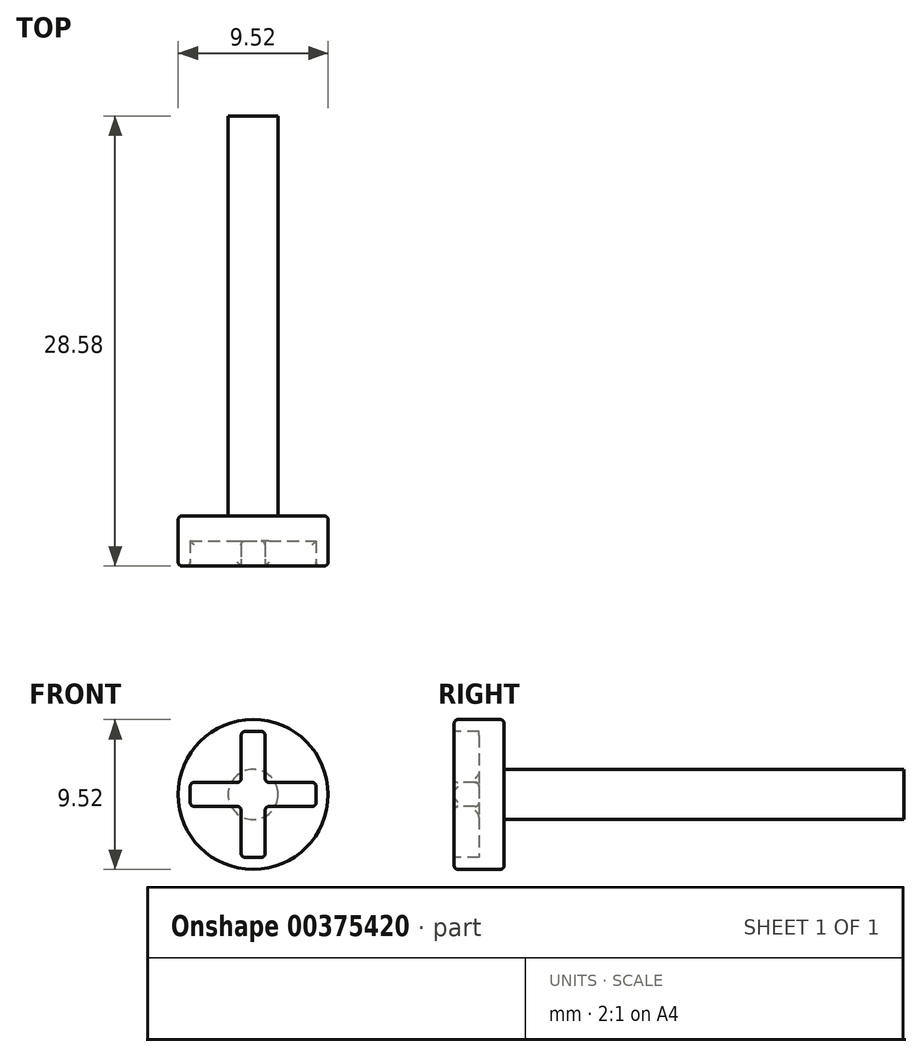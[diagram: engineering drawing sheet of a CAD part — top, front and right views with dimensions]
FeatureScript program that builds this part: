
annotation { "Feature Type Name" : "Feature", "Feature Type Description" : "" }
export const myFeature = defineFeature(function(context is Context, id is Id, definition is map)
    precondition{}
    {
        {
            var Q0;
            Q0=qCreatedBy(makeId("Front.planeOp"),FACE);
            var sketch = newSketch(context, id + "F0", { "sketchPlane" : qUnion([Q0])});
            skCircle(sketch, "E0", {"center": v(0, 0) * mm, "radius": 1.59 * mm});
            skSolve(sketch);
        }
        {
            var Q0;
            Q0=qSketchRegion(id+"F0",true);
            extrude(context, id + "F1", {"entities" : qUnion([Q0]), "depth" : 25.4 * mm, "symmetric" : true});
        }
        {
            var Q0;
            Q0=makeQuery(id+"F1.opExtrude","CAP_FACE",FACE,{"disambiguationData":[OSD([sQuery(id+"F0.wireOp",EDGE,"E0")])],"isStart":false});
            var sketch = newSketch(context, id + "F2", { "sketchPlane" : qUnion([Q0])});
            skCircle(sketch, "E1", {"center": v(0, 0) * mm, "radius": 4.76 * mm});
            skSolve(sketch);
        }
        {
            var Q0;
            Q0=qSketchRegion(id+"F2",true);
            extrude(context, id + "F3", {"entities" : qUnion([Q0]), "operationType" : NewBodyOperationType.ADD, "depth" : 3.17 * mm});
        }
        {
            var Q0;
            Q0=makeQuery(id+"F3.opExtrude","CAP_FACE",FACE,{"disambiguationData":[OSD([sQuery(id+"F2.wireOp",EDGE,"E1")])],"isStart":false});
            var sketch = newSketch(context, id + "F4", { "sketchPlane" : qUnion([Q0])});
            skLineSegment(sketch, "E2.bottom", {"start": v(-0.76, 4) * mm, "end": v(0.76, 4) * mm});
            skLineSegment(sketch, "E2.top", {"start": v(-0.76, -4) * mm, "end": v(0.76, -4) * mm});
            skLineSegment(sketch, "E2.left", {"start": v(-0.76, 4) * mm, "end": v(-0.76, -4) * mm});
            skLineSegment(sketch, "E2.right", {"start": v(0.76, 4) * mm, "end": v(0.76, -4) * mm});
            skLineSegment(sketch, "E3.bottom", {"start": v(-4, 0.76) * mm, "end": v(4, 0.76) * mm});
            skLineSegment(sketch, "E3.top", {"start": v(-4, -0.76) * mm, "end": v(4, -0.76) * mm});
            skLineSegment(sketch, "E3.left", {"start": v(-4, 0.76) * mm, "end": v(-4, -0.76) * mm});
            skLineSegment(sketch, "E3.right", {"start": v(4, 0.76) * mm, "end": v(4, -0.76) * mm});
            skSolve(sketch);
        }
        {
            var Q0;
            Q0=qSketchRegion(id+"F4",true);
            extrude(context, id + "F5", {"entities" : qUnion([Q0]), "operationType" : NewBodyOperationType.REMOVE, "oppositeDirection" : true, "depth" : 1.59 * mm});
        }
        {
            var Q0;
            Q0=makeQuery(id+"F3.opExtrude","CAP_EDGE",EDGE,{"disambiguationData":[OSD([sQuery(id+"F2.wireOp",EDGE,"E1")])],"isStart":false});
            var Q1;
            {var subQ0=sQuery(id+"F4.wireOp",EDGE,"E3.bottom");Q1=makeQuery(id+"F5.boolean.opBoolean","COPY",EDGE,{"derivedFrom":makeQuery(id+"F5.opExtrude","CAP_EDGE",EDGE,{"disambiguationData":[OSD([subQ0]),TDD([makeQuery(id+"F4.imprint","IMPRINT",EDGE,{"disambiguationData":[TD([[makeQuery(id+"F4.imprint","INTERSECT",VERTEX,{"derivedFrom":[subQ0,sQuery(id+"F4.wireOp",EDGE,"E3.left")]}),-1.0]])],"derivedFrom":subQ0})])],"isStart":true})});}
            var Q2;
            {var subQ0=sQuery(id+"F4.wireOp",EDGE,"E2.left");Q2=makeQuery(id+"F5.boolean.opBoolean","COPY",EDGE,{"derivedFrom":makeQuery(id+"F5.opExtrude","CAP_EDGE",EDGE,{"disambiguationData":[OSD([subQ0]),TDD([makeQuery(id+"F4.imprint","IMPRINT",EDGE,{"disambiguationData":[TD([[makeQuery(id+"F4.imprint","INTERSECT",VERTEX,{"derivedFrom":[sQuery(id+"F4.wireOp",EDGE,"E2.bottom"),subQ0]}),-1.0]])],"derivedFrom":subQ0})])],"isStart":true})});}
            var Q3;
            {var subQ0=sQuery(id+"F4.wireOp",EDGE,"E2.right");Q3=makeQuery(id+"F5.boolean.opBoolean","COPY",EDGE,{"derivedFrom":makeQuery(id+"F5.opExtrude","CAP_EDGE",EDGE,{"disambiguationData":[OSD([subQ0]),TDD([makeQuery(id+"F4.imprint","IMPRINT",EDGE,{"disambiguationData":[TD([[makeQuery(id+"F4.imprint","INTERSECT",VERTEX,{"derivedFrom":[sQuery(id+"F4.wireOp",EDGE,"E2.bottom"),subQ0]}),-1.0]])],"derivedFrom":subQ0})])],"isStart":true})});}
            var Q4;
            {var subQ0=sQuery(id+"F4.wireOp",EDGE,"E3.top");Q4=makeQuery(id+"F5.boolean.opBoolean","COPY",EDGE,{"derivedFrom":makeQuery(id+"F5.opExtrude","CAP_EDGE",EDGE,{"disambiguationData":[OSD([subQ0]),TDD([makeQuery(id+"F4.imprint","IMPRINT",EDGE,{"disambiguationData":[TD([[makeQuery(id+"F4.imprint","INTERSECT",VERTEX,{"derivedFrom":[subQ0,sQuery(id+"F4.wireOp",EDGE,"E3.left")]}),-1.0]])],"derivedFrom":subQ0})])],"isStart":true})});}
            var Q5;
            {var subQ0=sQuery(id+"F4.wireOp",EDGE,"E2.left");Q5=makeQuery(id+"F5.boolean.opBoolean","COPY",EDGE,{"derivedFrom":makeQuery(id+"F5.opExtrude","CAP_EDGE",EDGE,{"disambiguationData":[OSD([subQ0]),TDD([makeQuery(id+"F4.imprint","IMPRINT",EDGE,{"disambiguationData":[TD([[makeQuery(id+"F4.imprint","INTERSECT",VERTEX,{"derivedFrom":[sQuery(id+"F4.wireOp",EDGE,"E2.top"),subQ0]}),1.0]])],"derivedFrom":subQ0})])],"isStart":true})});}
            var Q6;
            {var subQ0=sQuery(id+"F4.wireOp",EDGE,"E3.top");Q6=makeQuery(id+"F5.boolean.opBoolean","COPY",EDGE,{"derivedFrom":makeQuery(id+"F5.opExtrude","CAP_EDGE",EDGE,{"disambiguationData":[OSD([subQ0]),TDD([makeQuery(id+"F4.imprint","IMPRINT",EDGE,{"disambiguationData":[TD([[makeQuery(id+"F4.imprint","INTERSECT",VERTEX,{"derivedFrom":[subQ0,sQuery(id+"F4.wireOp",EDGE,"E3.right")]}),1.0]])],"derivedFrom":subQ0})])],"isStart":true})});}
            var Q7;
            {var subQ0=sQuery(id+"F4.wireOp",EDGE,"E3.bottom");Q7=makeQuery(id+"F5.boolean.opBoolean","COPY",EDGE,{"derivedFrom":makeQuery(id+"F5.opExtrude","CAP_EDGE",EDGE,{"disambiguationData":[OSD([subQ0]),TDD([makeQuery(id+"F4.imprint","IMPRINT",EDGE,{"disambiguationData":[TD([[makeQuery(id+"F4.imprint","INTERSECT",VERTEX,{"derivedFrom":[subQ0,sQuery(id+"F4.wireOp",EDGE,"E3.right")]}),1.0]])],"derivedFrom":subQ0})])],"isStart":true})});}
            var Q8;
            {var subQ0=sQuery(id+"F4.wireOp",EDGE,"E3.bottom");Q8=makeQuery(id+"F5.boolean.opBoolean","COPY",FACE,{"derivedFrom":makeQuery(id+"F5.opExtrude","SWEPT_FACE",FACE,{"disambiguationData":[OSD([subQ0]),TDD([makeQuery(id+"F4.imprint","IMPRINT",EDGE,{"disambiguationData":[TD([[makeQuery(id+"F4.imprint","INTERSECT",VERTEX,{"derivedFrom":[subQ0,sQuery(id+"F4.wireOp",EDGE,"E3.left")]}),-1.0]])],"derivedFrom":subQ0})])]})});}
            var Q9;
            {var subQ0=sQuery(id+"F4.wireOp",EDGE,"E3.bottom");Q9=makeQuery(id+"F5.boolean.opBoolean","COPY",FACE,{"derivedFrom":makeQuery(id+"F5.opExtrude","SWEPT_FACE",FACE,{"disambiguationData":[OSD([subQ0]),TDD([makeQuery(id+"F4.imprint","IMPRINT",EDGE,{"disambiguationData":[TD([[makeQuery(id+"F4.imprint","INTERSECT",VERTEX,{"derivedFrom":[subQ0,sQuery(id+"F4.wireOp",EDGE,"E3.right")]}),1.0]])],"derivedFrom":subQ0})])]})});}
            var Q10;
            {var subQ0=sQuery(id+"F4.wireOp",EDGE,"E3.top");Q10=makeQuery(id+"F5.boolean.opBoolean","COPY",FACE,{"derivedFrom":makeQuery(id+"F5.opExtrude","SWEPT_FACE",FACE,{"disambiguationData":[OSD([subQ0]),TDD([makeQuery(id+"F4.imprint","IMPRINT",EDGE,{"disambiguationData":[TD([[makeQuery(id+"F4.imprint","INTERSECT",VERTEX,{"derivedFrom":[subQ0,sQuery(id+"F4.wireOp",EDGE,"E3.left")]}),-1.0]])],"derivedFrom":subQ0})])]})});}
            var Q11;
            {var subQ0=sQuery(id+"F4.wireOp",EDGE,"E3.top");Q11=makeQuery(id+"F5.boolean.opBoolean","COPY",FACE,{"derivedFrom":makeQuery(id+"F5.opExtrude","SWEPT_FACE",FACE,{"disambiguationData":[OSD([subQ0]),TDD([makeQuery(id+"F4.imprint","IMPRINT",EDGE,{"disambiguationData":[TD([[makeQuery(id+"F4.imprint","INTERSECT",VERTEX,{"derivedFrom":[subQ0,sQuery(id+"F4.wireOp",EDGE,"E3.right")]}),1.0]])],"derivedFrom":subQ0})])]})});}
            var Q12;
            Q12=makeQuery(id+"F5.boolean.opBoolean","COPY",EDGE,{"derivedFrom":makeQuery(id+"F5.opExtrude","CAP_EDGE",EDGE,{"disambiguationData":[OSD([sQuery(id+"F4.wireOp",EDGE,"E2.bottom")])],"isStart":true})});
            var Q13;
            Q13=makeQuery(id+"F5.boolean.opBoolean","COPY",EDGE,{"derivedFrom":makeQuery(id+"F5.opExtrude","CAP_EDGE",EDGE,{"disambiguationData":[OSD([sQuery(id+"F4.wireOp",EDGE,"E2.top")])],"isStart":true})});
            var Q14;
            Q14=makeQuery(id+"F5.boolean.opBoolean","COPY",EDGE,{"derivedFrom":makeQuery(id+"F5.opExtrude","SWEPT_EDGE",EDGE,{"disambiguationData":[OSD([sQuery(id+"F4.wireOp",EDGE,"E2.bottom"),sQuery(id+"F4.wireOp",EDGE,"E2.right")])]})});
            var Q15;
            Q15=makeQuery(id+"F5.boolean.opBoolean","COPY",EDGE,{"derivedFrom":makeQuery(id+"F5.opExtrude","SWEPT_EDGE",EDGE,{"disambiguationData":[OSD([sQuery(id+"F4.wireOp",EDGE,"E2.bottom"),sQuery(id+"F4.wireOp",EDGE,"E2.left")])]})});
            var Q16;
            Q16=makeQuery(id+"F5.boolean.opBoolean","COPY",EDGE,{"derivedFrom":makeQuery(id+"F5.opExtrude","SWEPT_EDGE",EDGE,{"disambiguationData":[OSD([sQuery(id+"F4.wireOp",EDGE,"E2.top"),sQuery(id+"F4.wireOp",EDGE,"E2.right")])]})});
            var Q17;
            Q17=makeQuery(id+"F5.boolean.opBoolean","COPY",EDGE,{"derivedFrom":makeQuery(id+"F5.opExtrude","SWEPT_EDGE",EDGE,{"disambiguationData":[OSD([sQuery(id+"F4.wireOp",EDGE,"E2.top"),sQuery(id+"F4.wireOp",EDGE,"E2.left")])]})});
            var Q18;
            Q18=makeQuery(id+"F3.opExtrude","CAP_EDGE",EDGE,{"disambiguationData":[OSD([sQuery(id+"F2.wireOp",EDGE,"E1")])],"isStart":true});
            fillet(context, id + "F6", {"entities" : qUnion([Q0, Q1, Q2, Q3, Q4, Q5, Q6, Q7, Q8, Q9, Q10, Q11, Q12, Q13, Q14, Q15, Q16, Q17, Q18]), "radius" : 0.25 * mm, "tangentPropagation" : true, "allowEdgeOverflow" : false});
        }
    });
